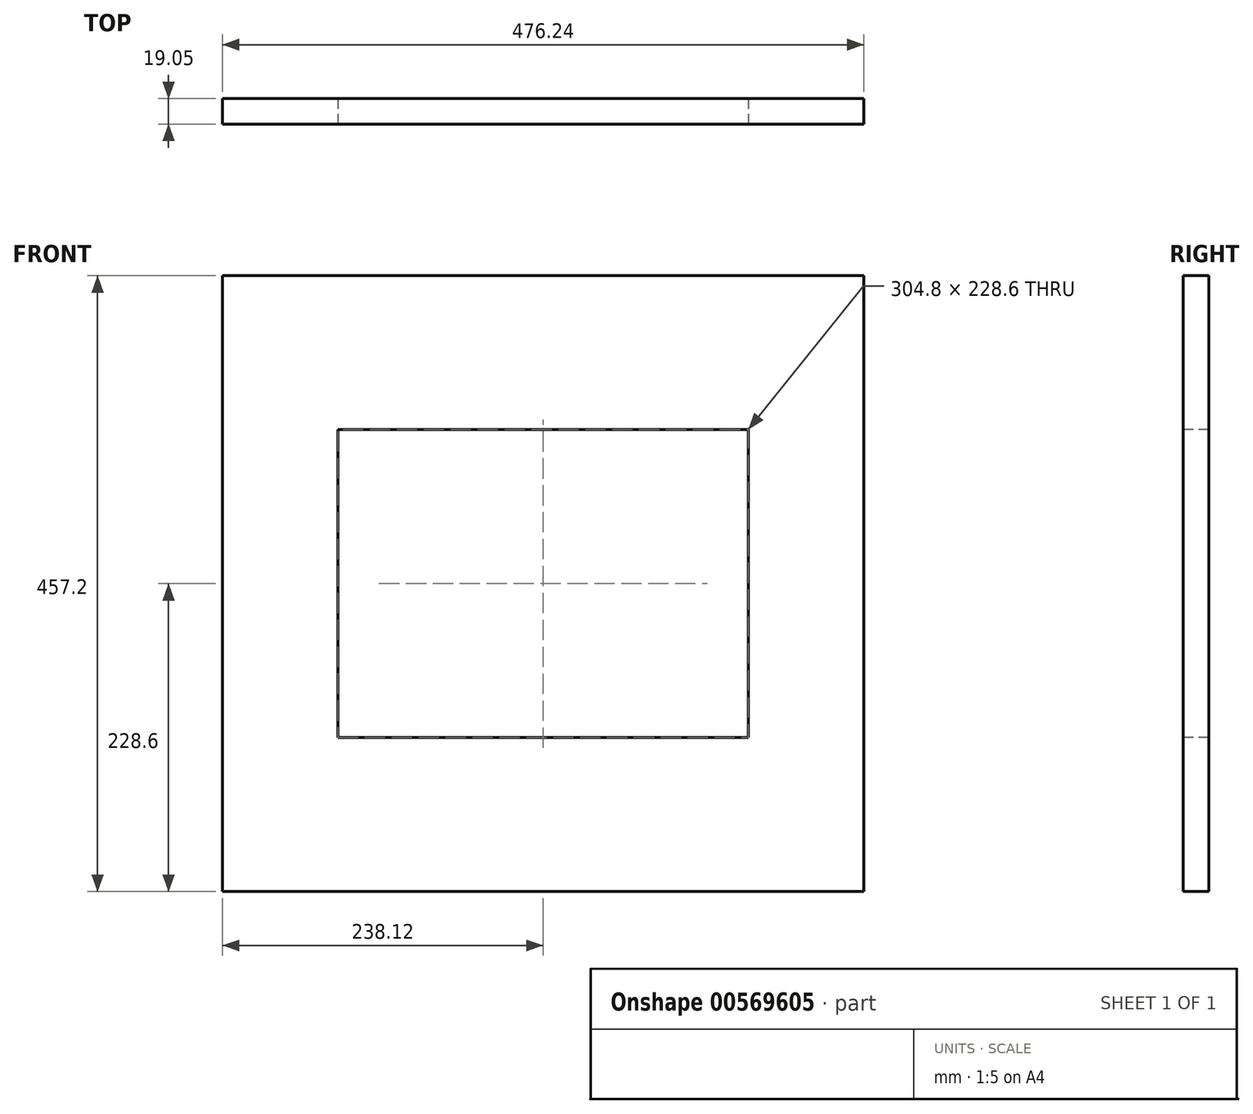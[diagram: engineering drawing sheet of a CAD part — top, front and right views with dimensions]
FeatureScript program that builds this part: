
annotation { "Feature Type Name" : "Feature", "Feature Type Description" : "" }
export const myFeature = defineFeature(function(context is Context, id is Id, definition is map)
    precondition{}
    {
        {
            var Q0;
            Q0=qCreatedBy(makeId("Front.planeOp"),FACE);
            var sketch = newSketch(context, id + "F0", { "sketchPlane" : qUnion([Q0])});
            skLineSegment(sketch, "E0.bottom", {"start": v(238.12, -228.6) * mm, "end": v(-238.13, -228.6) * mm});
            skLineSegment(sketch, "E0.top", {"start": v(238.13, 228.6) * mm, "end": v(-238.13, 228.6) * mm});
            skLineSegment(sketch, "E0.left", {"start": v(238.12, -228.6) * mm, "end": v(238.13, 228.6) * mm});
            skLineSegment(sketch, "E0.right", {"start": v(-238.13, -228.6) * mm, "end": v(-238.13, 228.6) * mm});
            skPoint(sketch, "E0.middle", {"position": v(0, 0) * mm});
            skSolve(sketch);
        }
        {
            var Q0;
            Q0=qSketchRegion(id+"F0",true);
            extrude(context, id + "F1", {"entities" : qUnion([Q0]), "depth" : 19.05 * mm, "offsetDistance" : 25.4 * mm});
        }
        {
            var Q0;
            Q0=makeQuery(id+"F1.opExtrude","CAP_FACE",FACE,{"disambiguationData":[OSD([sQuery(id+"F0.wireOp",EDGE,"E0.bottom"),sQuery(id+"F0.wireOp",EDGE,"E0.top"),sQuery(id+"F0.wireOp",EDGE,"E0.left"),sQuery(id+"F0.wireOp",EDGE,"E0.right")])],"isStart":false});
            var sketch = newSketch(context, id + "F2", { "sketchPlane" : qUnion([Q0])});
            skLineSegment(sketch, "E1.bottom", {"start": v(152.4, -114.3) * mm, "end": v(-152.4, -114.3) * mm});
            skLineSegment(sketch, "E1.top", {"start": v(152.4, 114.3) * mm, "end": v(-152.4, 114.3) * mm});
            skLineSegment(sketch, "E1.left", {"start": v(152.4, -114.3) * mm, "end": v(152.4, 114.3) * mm});
            skLineSegment(sketch, "E1.right", {"start": v(-152.4, -114.3) * mm, "end": v(-152.4, 114.3) * mm});
            skPoint(sketch, "E1.middle", {"position": v(0, 0) * mm});
            skSolve(sketch);
        }
        {
            var Q0;
            Q0=qSketchRegion(id+"F2",true);
            extrude(context, id + "F3", {"entities" : qUnion([Q0]), "operationType" : NewBodyOperationType.REMOVE, "oppositeDirection" : true, "depth" : 25.4 * mm, "offsetDistance" : 25.4 * mm});
        }
    });
